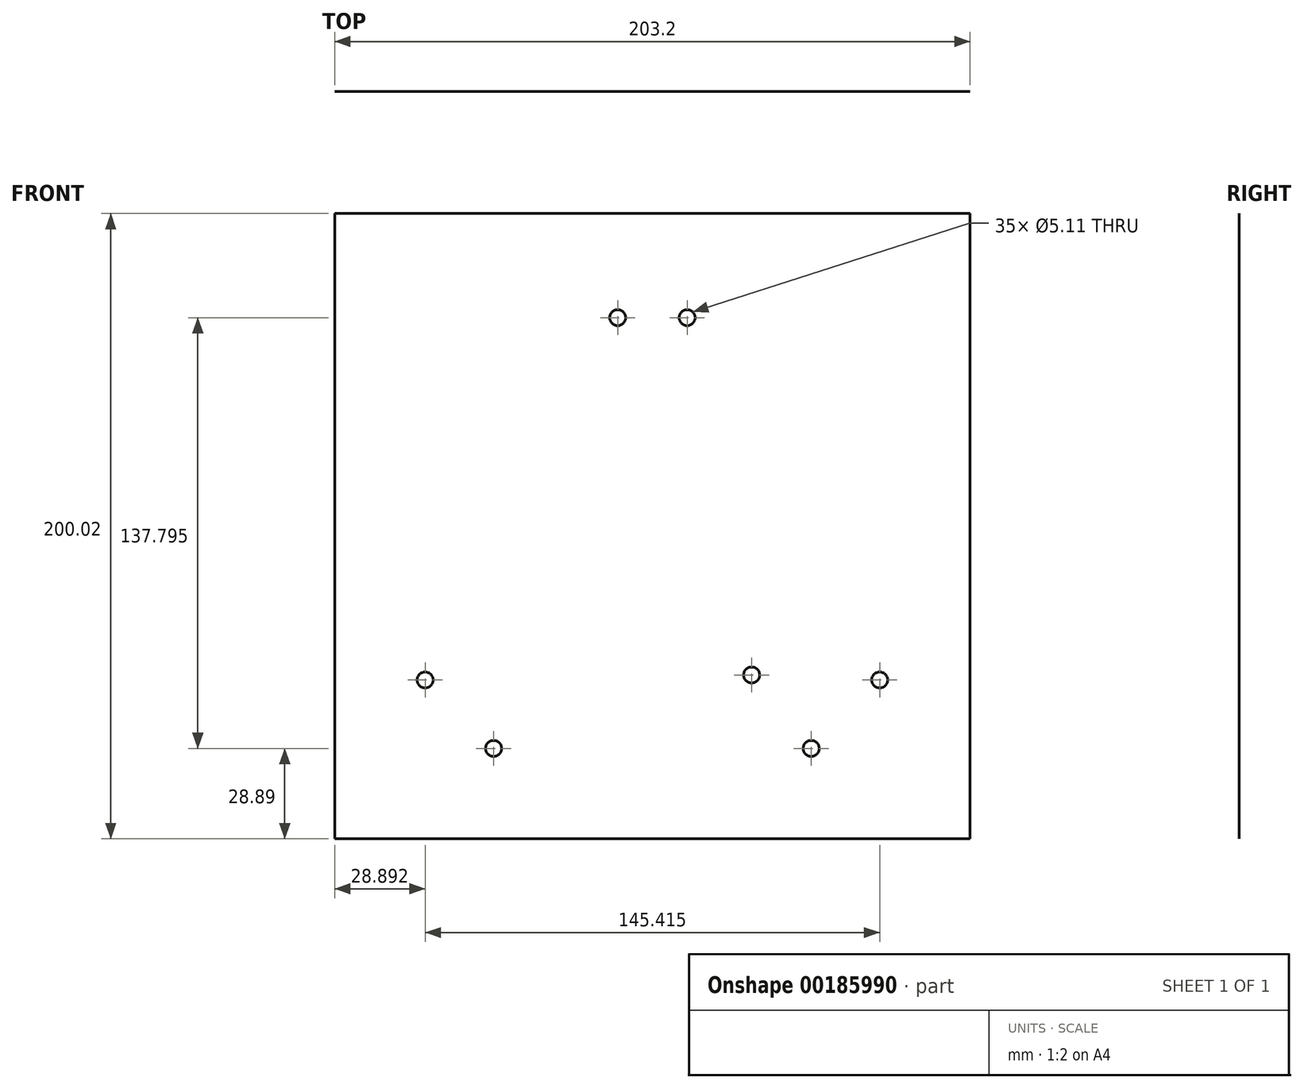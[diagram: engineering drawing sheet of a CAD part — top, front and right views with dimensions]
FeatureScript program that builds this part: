
annotation { "Feature Type Name" : "Feature", "Feature Type Description" : "" }
export const myFeature = defineFeature(function(context is Context, id is Id, definition is map)
    precondition{}
    {
        {
            var Q0;
            Q0=qCreatedBy(makeId("Front.planeOp"),FACE);
            var sketch = newSketch(context, id + "F0", { "sketchPlane" : qUnion([Q0])});
            skLineSegment(sketch, "E0.bottom", {"start": v(101.6, -100.01) * mm, "end": v(-101.6, -100.01) * mm});
            skLineSegment(sketch, "E0.top", {"start": v(101.6, 100.01) * mm, "end": v(-101.6, 100.01) * mm});
            skLineSegment(sketch, "E0.left", {"start": v(101.6, -100.01) * mm, "end": v(101.6, 100.01) * mm});
            skLineSegment(sketch, "E0.right", {"start": v(-101.6, -100.01) * mm, "end": v(-101.6, 100.01) * mm});
            skPoint(sketch, "E0.middle", {"position": v(0, 0) * mm});
            skSolve(sketch);
        }
        {
            var Q0;
            Q0 = qSketchRegion(id + "F0", true);
            extrude(context, id + "F1", {"entities" : qUnion([Q0]), "depth" : 1 / 203.2 * mm});
        }
        {
            var Q0;
            Q0=makeQuery(id+"F1.opExtrude","CAP_FACE",FACE,{"disambiguationData":[OSD([sQuery(id+"F0.wireOp",EDGE,"E0.bottom"),sQuery(id+"F0.wireOp",EDGE,"E0.top"),sQuery(id+"F0.wireOp",EDGE,"E0.left"),sQuery(id+"F0.wireOp",EDGE,"E0.right")])],"isStart":false});
            var sketch = newSketch(context, id + "F2", { "sketchPlane" : qUnion([Q0])});
            skPoint(sketch, "E1", {"position": v(-72.7, -49.21) * mm});
            skPoint(sketch, "E2", {"position": v(72.7, -49.21) * mm});
            skPoint(sketch, "E3", {"position": v(-50.8, -71.12) * mm});
            skPoint(sketch, "E4", {"position": v(50.8, -71.12) * mm});
            skPoint(sketch, "E5", {"position": v(31.75, -47.62) * mm});
            skPoint(sketch, "E6", {"position": v(-11.11, 66.67) * mm});
            skPoint(sketch, "E7", {"position": v(11.11, 66.67) * mm});
            skSolve(sketch);
        }
        {
            var Q0;
            Q0=sQuery(id+"F2.wireOp",VERTEX,"E1");
            var Q1;
            Q1=sQuery(id+"F2.wireOp",VERTEX,"E2");
            var Q2;
            Q2=sQuery(id+"F2.wireOp",VERTEX,"E3");
            var Q3;
            Q3=sQuery(id+"F2.wireOp",VERTEX,"E4");
            var Q4;
            Q4=sQuery(id+"F2.wireOp",VERTEX,"E5");
            var Q5;
            Q5=sQuery(id+"F2.wireOp",VERTEX,"E6");
            var Q6;
            Q6=sQuery(id+"F2.wireOp",VERTEX,"E7");
            var Q7;
            Q7=makeQuery(id+"F1.opExtrude","SWEPT_BODY",BODY,{"disambiguationData":[OSD([sQuery(id+"F0.wireOp",EDGE,"E0.bottom"),sQuery(id+"F0.wireOp",EDGE,"E0.top"),sQuery(id+"F0.wireOp",EDGE,"E0.left"),sQuery(id+"F0.wireOp",EDGE,"E0.right")])]});
            hole(context, id + "F3", {"style" : HoleStyle.SIMPLE, "endStyle" : HoleEndStyle.BLIND, "standardTappedOrClearance" : lookupTablePath({ "standard" : "ANSI", "fit" : "Normal (ASME)", "size" : "#10", "type" : "Clearance" }), "standardBlindInLast" : lookupTablePath({ "fit" : "Free", "standard" : "ANSI", "size" : "#10", "type" : "Clearance" }), "holeDiameter" : 5.1 * mm, "holeDepth" : 25 * mm, "locations" : qUnion([Q0, Q1, Q2, Q3, Q4, Q5, Q6]), "scope" : qUnion([Q7])});
        }
    });
